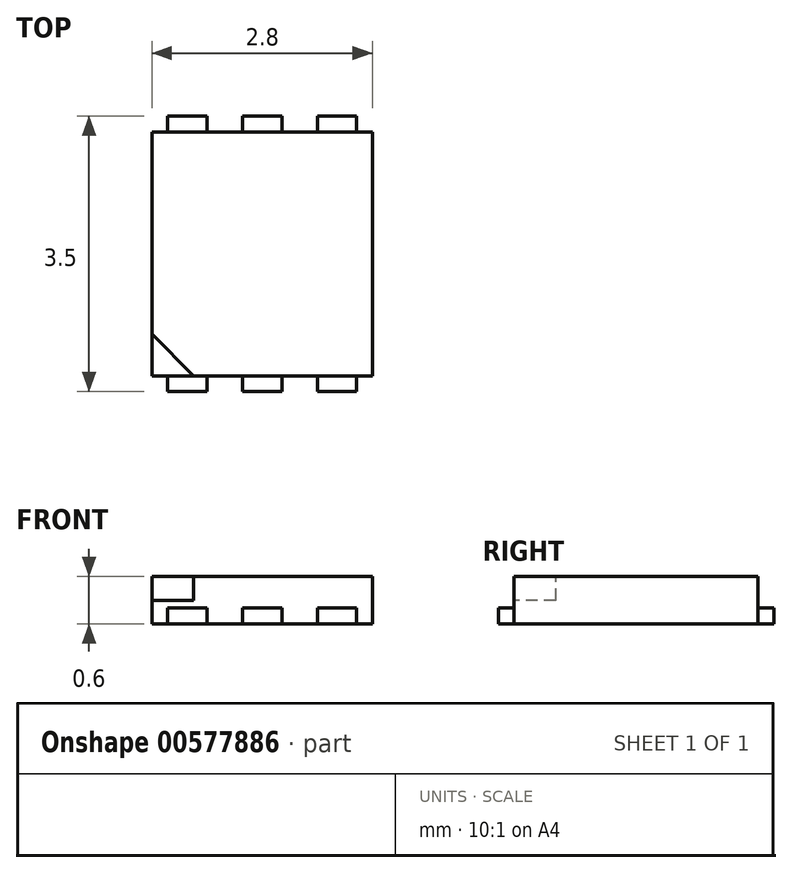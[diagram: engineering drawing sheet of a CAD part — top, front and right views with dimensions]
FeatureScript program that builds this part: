
annotation { "Feature Type Name" : "Feature", "Feature Type Description" : "" }
export const myFeature = defineFeature(function(context is Context, id is Id, definition is map)
    precondition{}
    {
        {
            var Q0;
            Q0=qCreatedBy(makeId("Top.planeOp"),FACE);
            var sketch = newSketch(context, id + "F0", { "sketchPlane" : qUnion([Q0])});
            skLineSegment(sketch, "E0.bottom", {"start": v(-1.07, 0) * mm, "end": v(1.73, 0) * mm});
            skLineSegment(sketch, "E0.top", {"start": v(-1.07, -3.1) * mm, "end": v(1.73, -3.1) * mm});
            skLineSegment(sketch, "E0.left", {"start": v(-1.07, 0) * mm, "end": v(-1.07, -3.1) * mm});
            skLineSegment(sketch, "E0.right", {"start": v(1.73, 0) * mm, "end": v(1.73, -3.1) * mm});
            skSolve(sketch);
        }
        {
            var Q0;
            Q0=makeQuery(id+"F0.imprint","IMPRINT",FACE,{"disambiguationData":[TD([[makeQuery(id+"F0.imprint","IMPRINT",EDGE,{"derivedFrom":sQuery(id+"F0.wireOp",EDGE,"E0.bottom")}),-1.0]])]});
            extrude(context, id + "F1", {"entities" : qUnion([Q0]), "depth" : .6 * mm, "offsetDistance" : 25 * mm});
        }
        {
            var Q0;
            Q0=makeQuery(id+"F1.opExtrude","CAP_FACE",FACE,{"disambiguationData":[OSD([sQuery(id+"F0.wireOp",EDGE,"E0.bottom"),sQuery(id+"F0.wireOp",EDGE,"E0.top"),sQuery(id+"F0.wireOp",EDGE,"E0.left"),sQuery(id+"F0.wireOp",EDGE,"E0.right")])],"isStart":false});
            var sketch = newSketch(context, id + "F2", { "sketchPlane" : qUnion([Q0])});
            skLineSegment(sketch, "E1", {"start": v(-1.07, -2.57) * mm, "end": v(-0.54, -3.1) * mm});
            skLineSegment(sketch, "E2", {"start": v(-0.54, -3.1) * mm, "end": v(-1.07, -3.1) * mm});
            skLineSegment(sketch, "E3", {"start": v(-1.07, -3.1) * mm, "end": v(-1.07, -2.57) * mm});
            skSolve(sketch);
        }
        {
            var Q0;
            Q0=makeQuery(id+"F2.imprint","IMPRINT",FACE,{"disambiguationData":[TD([[makeQuery(id+"F2.imprint","IMPRINT",EDGE,{"derivedFrom":sQuery(id+"F2.wireOp",EDGE,"E1")}),-1.0]])]});
            extrude(context, id + "F3", {"entities" : qUnion([Q0]), "operationType" : NewBodyOperationType.REMOVE, "oppositeDirection" : true, "depth" : .3 * mm, "offsetDistance" : 25 * mm});
        }
        {
            var Q0;
            Q0=makeQuery(id+"F1.opExtrude","CAP_FACE",FACE,{"disambiguationData":[OSD([sQuery(id+"F0.wireOp",EDGE,"E0.bottom"),sQuery(id+"F0.wireOp",EDGE,"E0.top"),sQuery(id+"F0.wireOp",EDGE,"E0.left"),sQuery(id+"F0.wireOp",EDGE,"E0.right")])],"isStart":true});
            var sketch = newSketch(context, id + "F4", { "sketchPlane" : qUnion([Q0])});
            skLineSegment(sketch, "E4.bottom", {"start": v(-0.87, 0.6) * mm, "end": v(-0.37, 0.6) * mm});
            skLineSegment(sketch, "E4.top", {"start": v(-0.87, -0.2) * mm, "end": v(-0.37, -0.2) * mm});
            skLineSegment(sketch, "E4.left", {"start": v(-0.87, 0.6) * mm, "end": v(-0.87, -0.2) * mm});
            skLineSegment(sketch, "E4.right", {"start": v(-0.37, 0.6) * mm, "end": v(-0.37, -0.2) * mm});
            skLineSegment(sketch, "E5.bottom", {"start": v(0.08, 0.6) * mm, "end": v(0.58, 0.6) * mm});
            skLineSegment(sketch, "E5.top", {"start": v(0.08, -0.2) * mm, "end": v(0.58, -0.2) * mm});
            skLineSegment(sketch, "E5.left", {"start": v(0.08, 0.6) * mm, "end": v(0.08, -0.2) * mm});
            skLineSegment(sketch, "E5.right", {"start": v(0.58, 0.6) * mm, "end": v(0.58, -0.2) * mm});
            skLineSegment(sketch, "E6.bottom", {"start": v(1.03, 0.6) * mm, "end": v(1.53, 0.6) * mm});
            skLineSegment(sketch, "E6.top", {"start": v(1.03, -0.2) * mm, "end": v(1.53, -0.2) * mm});
            skLineSegment(sketch, "E6.left", {"start": v(1.03, 0.6) * mm, "end": v(1.03, -0.2) * mm});
            skLineSegment(sketch, "E6.right", {"start": v(1.53, 0.6) * mm, "end": v(1.53, -0.2) * mm});
            skLineSegment(sketch, "E7.bottom", {"start": v(1.03, 2.5) * mm, "end": v(1.53, 2.5) * mm});
            skLineSegment(sketch, "E7.top", {"start": v(1.03, 3.3) * mm, "end": v(1.53, 3.3) * mm});
            skLineSegment(sketch, "E7.left", {"start": v(1.03, 2.5) * mm, "end": v(1.03, 3.3) * mm});
            skLineSegment(sketch, "E7.right", {"start": v(1.53, 2.5) * mm, "end": v(1.53, 3.3) * mm});
            skLineSegment(sketch, "E8.bottom", {"start": v(0.08, 2.5) * mm, "end": v(0.58, 2.5) * mm});
            skLineSegment(sketch, "E8.top", {"start": v(0.08, 3.3) * mm, "end": v(0.58, 3.3) * mm});
            skLineSegment(sketch, "E8.left", {"start": v(0.08, 2.5) * mm, "end": v(0.08, 3.3) * mm});
            skLineSegment(sketch, "E8.right", {"start": v(0.58, 2.5) * mm, "end": v(0.58, 3.3) * mm});
            skLineSegment(sketch, "E9.bottom", {"start": v(-0.87, 3.3) * mm, "end": v(-0.37, 3.3) * mm});
            skLineSegment(sketch, "E9.top", {"start": v(-0.87, 2.5) * mm, "end": v(-0.37, 2.5) * mm});
            skLineSegment(sketch, "E9.left", {"start": v(-0.87, 3.3) * mm, "end": v(-0.87, 2.5) * mm});
            skLineSegment(sketch, "E9.right", {"start": v(-0.37, 3.3) * mm, "end": v(-0.37, 2.5) * mm});
            skSolve(sketch);
        }
        {
            var Q0;
            Q0 = qSketchRegion(id + "F4", true);
            extrude(context, id + "F5", {"entities" : qUnion([Q0]), "operationType" : NewBodyOperationType.ADD, "oppositeDirection" : true, "depth" : .2 * mm, "offsetDistance" : 25 * mm});
        }
    });
